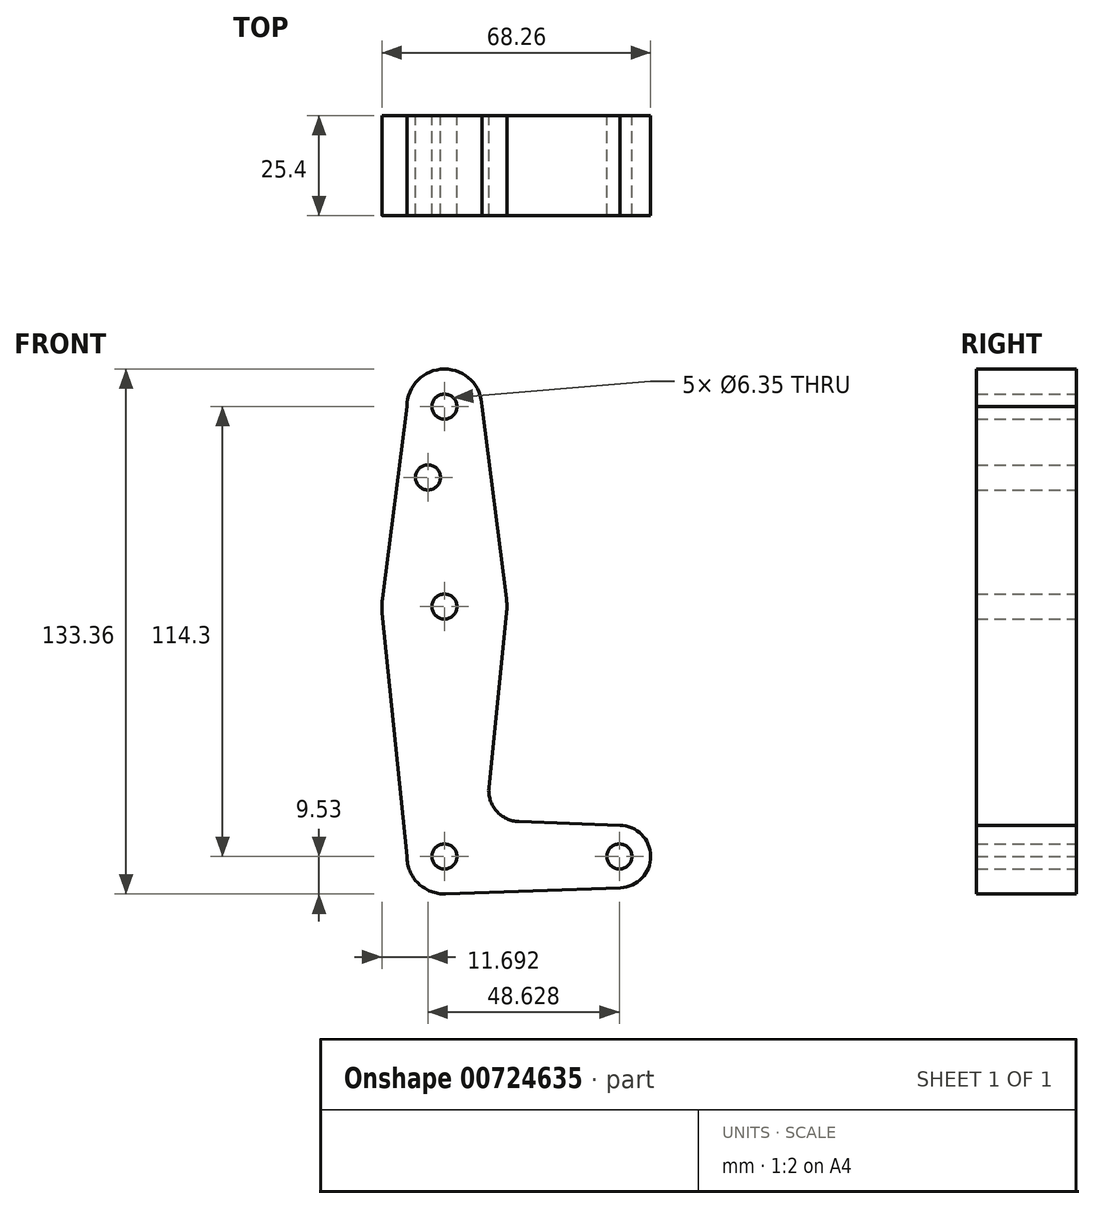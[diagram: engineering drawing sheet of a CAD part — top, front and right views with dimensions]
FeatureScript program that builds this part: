
annotation { "Feature Type Name" : "Feature", "Feature Type Description" : "" }
export const myFeature = defineFeature(function(context is Context, id is Id, definition is map)
    precondition{}
    {
        {
            var Q0;
            Q0=qCreatedBy(makeId("Front.planeOp"),FACE);
            var sketch = newSketch(context, id + "F0", { "sketchPlane" : qUnion([Q0])});
            skLineSegment(sketch, "E0", {"start": v(0, 0) * mm, "end": v(0, 114.3) * mm});
            skLineSegment(sketch, "E1", {"start": v(0, 114.3) * mm, "end": v(0, 0) * mm, "construction": true});
            skLineSegment(sketch, "E2", {"start": v(44.45, 0) * mm, "end": v(0, 0) * mm, "construction": true});
            skCircle(sketch, "E3", {"center": v(0, 114.3) * mm, "radius": 9.53 * mm});
            skCircle(sketch, "E4", {"center": v(0, 63.5) * mm, "radius": 15.88 * mm});
            skCircle(sketch, "E5", {"center": v(0, 0) * mm, "radius": 9.53 * mm});
            skCircle(sketch, "E6", {"center": v(44.45, 0) * mm, "radius": 7.94 * mm});
            skLineSegment(sketch, "E7", {"start": v(-9.53, 0) * mm, "end": v(-15.8, 61.9) * mm});
            skLineSegment(sketch, "E8", {"start": v(-9.53, 114.3) * mm, "end": v(-15.75, 65.5) * mm});
            skLineSegment(sketch, "E9", {"start": v(9.52, 114.3) * mm, "end": v(15.75, 65.5) * mm});
            skCircle(sketch, "E10", {"center": v(-4.18, 96.3) * mm, "radius": 3.18 * mm});
            skCircle(sketch, "E11", {"center": v(0, 63.5) * mm, "radius": 3.18 * mm});
            skCircle(sketch, "E12", {"center": v(0, 114.3) * mm, "radius": 3.18 * mm});
            skCircle(sketch, "E13", {"center": v(0, 0) * mm, "radius": 3.18 * mm});
            skCircle(sketch, "E14", {"center": v(44.45, 0) * mm, "radius": 3.18 * mm});
            skLineSegment(sketch, "E15", {"start": v(44.73, -7.93) * mm, "end": v(0.19, -9.52) * mm});
            skPoint(sketch, "E16.newPointA", {"position": v(44.6, 7.94) * mm});
            skLineSegment(sketch, "E17", {"start": v(15.8, 61.9) * mm, "end": v(11.3, 17.6) * mm});
            skLineSegment(sketch, "E18", {"start": v(44.6, 7.94) * mm, "end": v(18.93, 8.85) * mm});
            skPoint(sketch, "E19.newPointA", {"position": v(0, 9.53) * mm});
            skPoint(sketch, "E19.newPointB", {"position": v(9.52, 0) * mm});
            skArc(sketch, "E19.filletArc", {"start": v(11.3, 17.6) * mm, "mid": v(13.22, 11.57) * mm, "end": v(18.93, 8.85) * mm});
            skSolve(sketch);
        }
        {
            var Q0;
            Q0 = qSketchRegion(id + "F0", true);
            extrude(context, id + "F1", {"entities" : qUnion([Q0]), "depth" : 25.4 * mm, "offsetDistance" : 25.4 * mm});
        }
    });
